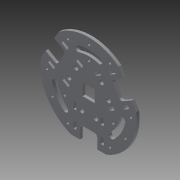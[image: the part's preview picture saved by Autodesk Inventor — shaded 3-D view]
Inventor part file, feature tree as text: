
AUTODESK INVENTOR PART (.ipt)
format: ipt  version: 2015 (Build 190159000, 159)  size: 414,208 bytes
history: native  units: mm
features: extrude x7, sketch x7, pattern_circular x3, projected_geometry x3, fillet x1
ambient origin geometry x8: Origin, YZ Plane, XZ Plane, XY Plane, X Axis, Y Axis, Z Axis, Center Point
bodies: Solid1 (feature_tree)
feature tree (21):
  extrude  "Extrusion1"  Depth=47.907mm
  sketch  "Sketch2"  dims[d2=120.0deg d3=120.0deg]
  sketch  "Sketch3"  dims[d4=47.907mm d5=47.907mm]
  extrude  "Extrusion2"  TaperAngle=120.0deg  [1 undecoded]
  extrude  "Extrusion3"  Depth=47.907mm
  extrude  "Extrusion4"  Depth=51.5mm
  extrude  "Extrusion5"  Depth=3.0mm TaperAngle=0.0deg
  pattern_circular  "Circular Pattern1"  [2 undecoded]
  extrude  "Extrusion6"  Depth=3.0mm
  extrude  "Extrusion7"  Depth=7.0mm
  pattern_circular  "Circular Pattern2"  [2 undecoded]
  fillet  "Fillet1"  Radius=11.0mm
  pattern_circular  "Circular Pattern3"  [2 undecoded]
  sketch  "Sketch1"  dims[d0=100.0mm d1=47.907mm]
  projected_geometry  "Projected Loop1"
  sketch  "Sketch4"  dims[d6=51.5mm d7=51.5mm]
  sketch  "Sketch5"  dims[d8=51.5mm d9=3.0mm d10=0.0mm]
  sketch  "Sketch6"  dims[d11=5.0mm]
  projected_geometry  "Projected Loop2"
  sketch  "Sketch7"  dims[d12=5.0mm d13=20.006mm d14=15.0mm d15=7.0mm d16=7.0mm d17=11.0mm d18=7.0mm d19=32.0mm d20=3.0mm d21=3.0mm d22=3.0mm d23=0.0mm d24=3.0mm d25=0.0mm d26=18.5mm d28=14.0mm d29=3.0mm d30=0.0mm d31=12.8mm d32=12.8mm d33=3.0mm d34=0.0mm d35=30.0mm d36=360.0deg d38=3.0mm d39=3.0mm d40=3.0mm d41=120.0deg d42=120.0deg d43=90.0mm d44=60.0mm d45=3.0mm d46=3.0mm d47=3.0mm d48=3.0mm d49=0.0mm d50=7.330383mm d51=7.330383mm d52=6.0mm d53=34.0mm d54=3.0mm d55=0.0mm d56=30.0mm d57=360.0deg d59=3.0mm d60=30.0mm d61=360.0deg d63=3.0mm d64=3.0mm d65=3.0mm d66=3.0mm d67=30.0deg d68=30.0deg d69=30.0deg d70=30.0deg d71=30.0deg d72=30.0deg d73=3.0mm d74=3.0mm]
  projected_geometry  "Projected Loop3"
note: 7 required parameter values undecoded (feature->parameter linkage not recoverable at this tier; creation-order binding heuristic only, values carry confidence <= 0.55)
